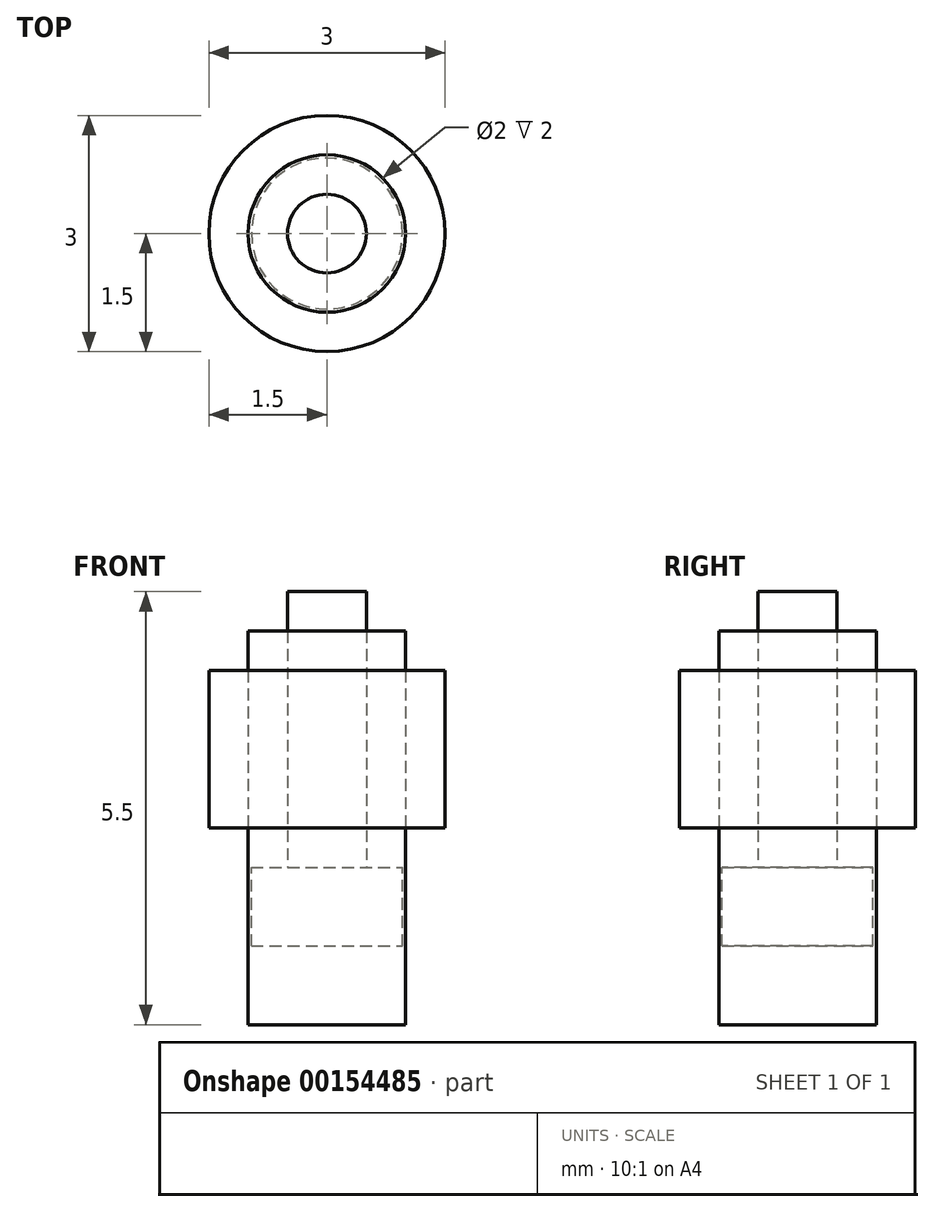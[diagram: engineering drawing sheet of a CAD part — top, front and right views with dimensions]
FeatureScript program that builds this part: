
annotation { "Feature Type Name" : "Feature", "Feature Type Description" : "" }
export const myFeature = defineFeature(function(context is Context, id is Id, definition is map)
    precondition{}
    {
        {
            var Q0;
            Q0=qCreatedBy(makeId("Top.planeOp"),FACE);
            var sketch = newSketch(context, id + "F0", { "sketchPlane" : qUnion([Q0])});
            skCircle(sketch, "E0", {"center": v(0, 0) * mm, "radius": 0.5 * mm});
            skCircle(sketch, "E1", {"center": v(0, 0) * mm, "radius": 1 * mm});
            skCircle(sketch, "E2", {"center": v(0, 0) * mm, "radius": 1.5 * mm});
            skSolve(sketch);
        }
        {
            var Q0;
            Q0=makeQuery(id+"F0.imprint","IMPRINT",FACE,{"disambiguationData":[TD([[makeQuery(id+"F0.imprint","IMPRINT",EDGE,{"derivedFrom":sQuery(id+"F0.wireOp",EDGE,"E0")}),1.0]])]});
            extrude(context, id + "F1", {"entities" : qUnion([Q0]), "depth" : 3 * mm});
        }
        {
            var Q0;
            Q0=makeQuery(id+"F0.imprint","IMPRINT",FACE,{"disambiguationData":[TD([[makeQuery(id+"F0.imprint","IMPRINT",EDGE,{"derivedFrom":sQuery(id+"F0.wireOp",EDGE,"E1")}),-1.0]])]});
            extrude(context, id + "F2", {"entities" : qUnion([Q0]), "depth" : 2 * mm});
        }
        {
            var Q0;
            Q0=makeQuery(id+"F0.imprint","IMPRINT",FACE,{"disambiguationData":[TD([[makeQuery(id+"F0.imprint","IMPRINT",EDGE,{"derivedFrom":sQuery(id+"F0.wireOp",EDGE,"E0")}),1.0]])]});
            extrude(context, id + "F3", {"entities" : qUnion([Q0]), "operationType" : NewBodyOperationType.ADD, "oppositeDirection" : true, "depth" : 1 * mm});
        }
        {
            var Q0;
            Q0=makeQuery(id+"F3.opExtrude","CAP_FACE",FACE,{"disambiguationData":[OSD([sQuery(id+"F0.wireOp",EDGE,"E0")])],"isStart":false});
            var sketch = newSketch(context, id + "F4", { "sketchPlane" : qUnion([Q0])});
            skCircle(sketch, "E3", {"center": v(0, 0) * mm, "radius": 0.96 * mm});
            skSolve(sketch);
        }
        {
            var Q0;
            Q0 = qSketchRegion(id + "F4", true);
            extrude(context, id + "F5", {"entities" : qUnion([Q0]), "operationType" : NewBodyOperationType.ADD, "endBound" : BoundingType.SYMMETRIC, "depth" : 1 * mm});
        }
        {
            var Q0;
            Q0=qCreatedBy(makeId("Top.planeOp"),FACE);
            var sketch = newSketch(context, id + "F6", { "sketchPlane" : qUnion([Q0])});
            skCircle(sketch, "E4", {"center": v(0, 0) * mm, "radius": 1 * mm});
            skSolve(sketch);
        }
        {
            var Q0;
            Q0 = qSketchRegion(id + "F6", true);
            extrude(context, id + "F7", {"entities" : qUnion([Q0]), "endBound" : BoundingType.SYMMETRIC, "depth" : 5 * mm});
        }
    });
